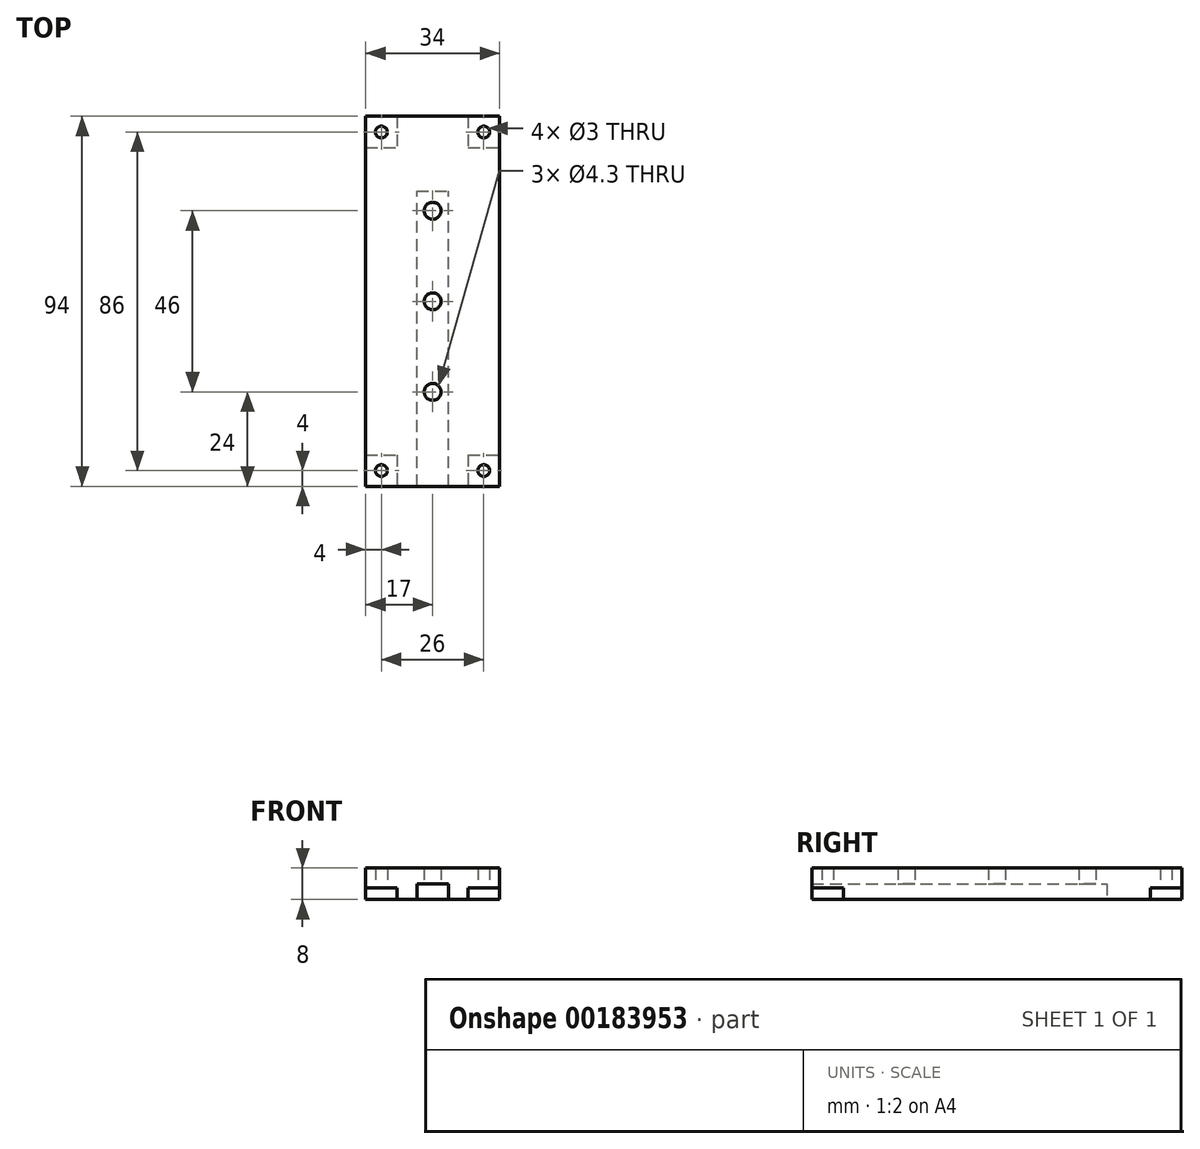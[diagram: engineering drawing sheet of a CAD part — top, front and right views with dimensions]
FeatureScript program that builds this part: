
annotation { "Feature Type Name" : "Feature", "Feature Type Description" : "" }
export const myFeature = defineFeature(function(context is Context, id is Id, definition is map)
    precondition{}
    {
        {
            var Q0;
            Q0=qCreatedBy(makeId("Top.planeOp"),FACE);
            var sketch = newSketch(context, id + "F0", { "sketchPlane" : qUnion([Q0])});
            skLineSegment(sketch, "E0.bottom", {"start": v(-17, 47) * mm, "end": v(17, 47) * mm});
            skLineSegment(sketch, "E0.top", {"start": v(-17, -47) * mm, "end": v(17, -47) * mm});
            skLineSegment(sketch, "E0.left", {"start": v(-17, 47) * mm, "end": v(-17, -47) * mm});
            skLineSegment(sketch, "E0.right", {"start": v(17, 47) * mm, "end": v(17, -47) * mm});
            skCircle(sketch, "E1", {"center": v(0, 23) * mm, "radius": 2.15 * mm});
            skCircle(sketch, "E2", {"center": v(0, -23) * mm, "radius": 2.15 * mm});
            skCircle(sketch, "E3", {"center": v(0, 0) * mm, "radius": 2.15 * mm});
            skCircle(sketch, "E4", {"center": v(-13, 43) * mm, "radius": 1.5 * mm});
            skCircle(sketch, "E5", {"center": v(13, 43) * mm, "radius": 1.5 * mm});
            skCircle(sketch, "E6", {"center": v(-13, -43) * mm, "radius": 1.5 * mm});
            skCircle(sketch, "E7", {"center": v(13, -43) * mm, "radius": 1.5 * mm});
            skSolve(sketch);
        }
        {
            var Q0;
            Q0 = qSketchRegion(id + "F0", true);
            extrude(context, id + "F1", {"entities" : qUnion([Q0]), "depth" : 8 * mm});
        }
        {
            var Q0;
            Q0=qCreatedBy(makeId("Top.planeOp"),FACE);
            var sketch = newSketch(context, id + "F2", { "sketchPlane" : qUnion([Q0])});
            skLineSegment(sketch, "E8.bottom", {"start": v(-17, 47) * mm, "end": v(-9, 47) * mm});
            skLineSegment(sketch, "E8.top", {"start": v(-17, 39) * mm, "end": v(-9, 39) * mm});
            skLineSegment(sketch, "E8.left", {"start": v(-17, 47) * mm, "end": v(-17, 39) * mm});
            skLineSegment(sketch, "E8.right", {"start": v(-9, 47) * mm, "end": v(-9, 39) * mm});
            skLineSegment(sketch, "E9.bottom", {"start": v(9, 47) * mm, "end": v(17, 47) * mm});
            skLineSegment(sketch, "E9.top", {"start": v(9, 39) * mm, "end": v(17, 39) * mm});
            skLineSegment(sketch, "E9.left", {"start": v(9, 47) * mm, "end": v(9, 39) * mm});
            skLineSegment(sketch, "E9.right", {"start": v(17, 47) * mm, "end": v(17, 39) * mm});
            skLineSegment(sketch, "E10.bottom", {"start": v(-17, -39) * mm, "end": v(-9, -39) * mm});
            skLineSegment(sketch, "E10.top", {"start": v(-17, -47) * mm, "end": v(-9, -47) * mm});
            skLineSegment(sketch, "E10.left", {"start": v(-17, -39) * mm, "end": v(-17, -47) * mm});
            skLineSegment(sketch, "E10.right", {"start": v(-9, -39) * mm, "end": v(-9, -47) * mm});
            skLineSegment(sketch, "E11.bottom", {"start": v(9, -39) * mm, "end": v(17, -39) * mm});
            skLineSegment(sketch, "E11.top", {"start": v(9, -47) * mm, "end": v(17, -47) * mm});
            skLineSegment(sketch, "E11.left", {"start": v(9, -39) * mm, "end": v(9, -47) * mm});
            skLineSegment(sketch, "E11.right", {"start": v(17, -39) * mm, "end": v(17, -47) * mm});
            skSolve(sketch);
        }
        {
            var Q0;
            Q0 = qSketchRegion(id + "F2", true);
            extrude(context, id + "F3", {"entities" : qUnion([Q0]), "operationType" : NewBodyOperationType.REMOVE, "depth" : 3 * mm});
        }
        {
            var Q0;
            Q0=qCreatedBy(makeId("Front.planeOp"),FACE);
            var sketch = newSketch(context, id + "F4", { "sketchPlane" : qUnion([Q0])});
            skLineSegment(sketch, "E12.bottom", {"start": v(-4, 4) * mm, "end": v(4, 4) * mm});
            skLineSegment(sketch, "E12.top", {"start": v(-4, -1.47) * mm, "end": v(4, -1.47) * mm});
            skLineSegment(sketch, "E12.left", {"start": v(-4, 4) * mm, "end": v(-4, -1.47) * mm});
            skLineSegment(sketch, "E12.right", {"start": v(4, 4) * mm, "end": v(4, -1.47) * mm});
            skSolve(sketch);
        }
        {
            var Q0;
            Q0 = qSketchRegion(id + "F4", true);
            extrude(context, id + "F5", {"entities" : qUnion([Q0]), "operationType" : NewBodyOperationType.REMOVE, "depth" : 100 * mm, "hasSecondDirection" : true, "secondDirectionOppositeDirection" : true, "secondDirectionDepth" : 28 * mm});
        }
    });
